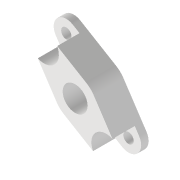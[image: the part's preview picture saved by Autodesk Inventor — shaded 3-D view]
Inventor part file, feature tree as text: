
AUTODESK INVENTOR PART (.ipt)
format: ipt  version: 2022 (Build 260153000, 153)  size: 141,312 bytes
history: native  units: mm
features: reference x6, sketch x4, extrude x3, other x2, hole x1, projected_geometry x1
ambient origin geometry x8: Origin, YZ Plane, XZ Plane, XY Plane, X Axis, Y Axis, Z Axis, Center Point
bodies: Volumenkörper1 (feature_tree)
feature tree (17):
  extrude  "Extrusion1"  Depth=2.0mm
  extrude  "Extrusion2"  Depth=6.7mm
  extrude  "Extrusion3"  [1 undecoded]
  hole  "Bohrung1"  [1 undecoded]
  sketch  "Skizze1"  dims[d0=8.0mm d1=0.0mm d2=2.0mm]
  reference  "Referenz1"
  reference  "Referenz2"
  reference  "Referenz3"
  sketch  "Skizze2"  dims[d3=3.0mm d4=0.0mm d5=6.7mm]
  projected_geometry  "Projizierte Kontur1"
  sketch  "Skizze3"  dims[d6=3.0mm d7=0.0mm]
  reference  "Referenz4"
  reference  "Referenz5"
  reference  "Referenz6"
  sketch  "Skizze4"  dims[d8=2.8mm d9=6.0mm d10=8.0mm d11=6.0mm d12=90.0deg d13=8.0mm d14=20.594885mm]
  other  "Assembly_Matchboxscope_injectionmolded.iam"
  other  "IM_Matchboxscope_base:1"
note: 2 required parameter values undecoded (feature->parameter linkage not recoverable at this tier; creation-order binding heuristic only, values carry confidence <= 0.55)
